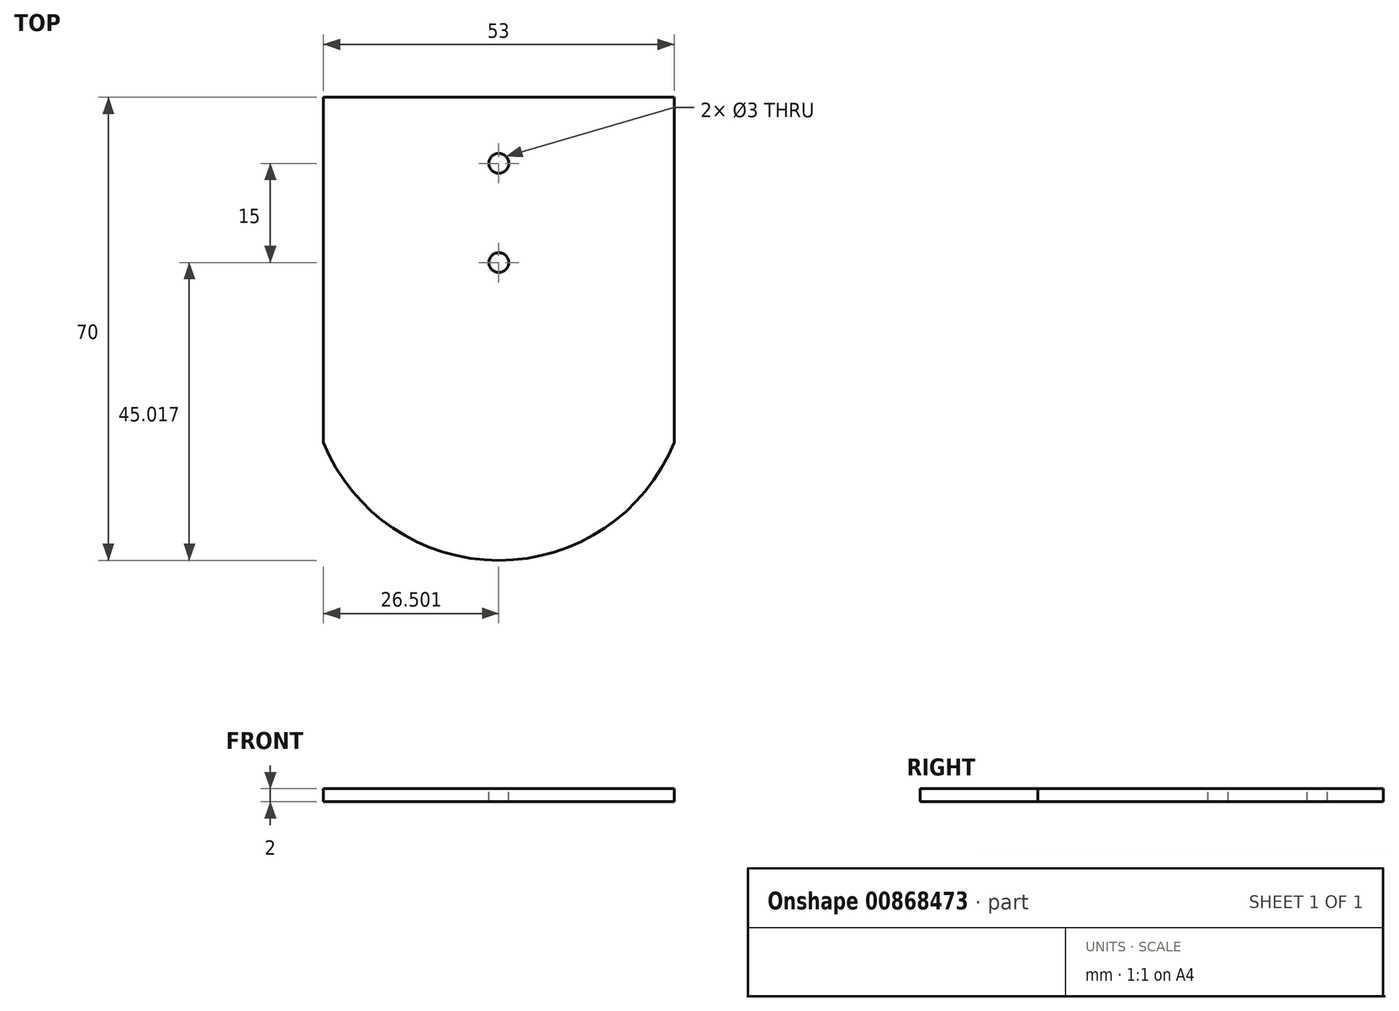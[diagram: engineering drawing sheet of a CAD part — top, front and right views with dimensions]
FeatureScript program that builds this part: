
annotation { "Feature Type Name" : "Feature", "Feature Type Description" : "" }
export const myFeature = defineFeature(function(context is Context, id is Id, definition is map)
    precondition{}
    {
        {
            var Q0;
            Q0=qCreatedBy(makeId("Top.planeOp"), FACE);
            var sketch = newSketch(context, id + "F0", { "sketchPlane" : qUnion([Q0])});
            skLineSegment(sketch, "E0", {"start": v(-38.9, 16.27) * mm, "end": v(14.1, 16.27) * mm});
            skLineSegment(sketch, "E1", {"start": v(-12.4, 16.27) * mm, "end": v(-12.4, -53.73) * mm, "construction": true});
            skLineSegment(sketch, "E2", {"start": v(-38.9, 16.27) * mm, "end": v(-38.9, -35.93) * mm});
            skLineSegment(sketch, "E3", {"start": v(14.1, 16.27) * mm, "end": v(14.1, -35.93) * mm});
            skPoint(sketch, "E4", {"position": v(-38.9, -35.93) * mm});
            skLineSegment(sketch, "E5", {"start": v(-38.9, -35.93) * mm, "end": v(14.1, -35.93) * mm, "construction": true});
            skArc(sketch, "E6", {"start": v(-38.9, -35.93) * mm, "mid": v(-12.4, -53.73) * mm, "end": v(14.1, -35.93) * mm});
            skPoint(sketch, "E7.orphan", {"position": v(-38.9, -53.73) * mm});
            skPoint(sketch, "E8.orphan", {"position": v(14.1, -53.73) * mm});
            skCircle(sketch, "E9", {"center": v(-12.4, 6.29) * mm, "radius": 1.5 * mm});
            skCircle(sketch, "E10", {"center": v(-12.4, -8.71) * mm, "radius": 1.5 * mm});
            skArc(sketch, "E11", {"start": v(-6.57, 9.18) * mm, "mid": v(-6.19, 10.88) * mm, "end": v(-6.42, 12.62) * mm, "construction": true});
            skLineSegment(sketch, "E12", {"start": v(-6.42, 12.62) * mm, "end": v(-7.1, 14.76) * mm, "construction": true});
            skArc(sketch, "E13", {"start": v(-22.4, 6.29) * mm, "mid": v(-17.25, 15.04) * mm, "end": v(-7.1, 14.76) * mm, "construction": true});
            skLineSegment(sketch, "E14", {"start": v(-22.4, -8.71) * mm, "end": v(-22.4, 6.29) * mm, "construction": true});
            skArc(sketch, "E15", {"start": v(-2.4, -8.71) * mm, "mid": v(-12.4, -18.71) * mm, "end": v(-22.4, -8.71) * mm, "construction": true});
            skLineSegment(sketch, "E16", {"start": v(-2.4, -8.71) * mm, "end": v(-2.4, 6.29) * mm, "construction": true});
            skArc(sketch, "E17", {"start": v(-2.6, 8.28) * mm, "mid": v(-2.46, 7.29) * mm, "end": v(-2.4, 6.29) * mm, "construction": true});
            skLineSegment(sketch, "E18", {"start": v(-7.02, -2.3) * mm, "end": v(-2.6, 8.28) * mm, "construction": true});
            skArc(sketch, "E19", {"start": v(-7.02, -2.3) * mm, "mid": v(-7.31, -3.25) * mm, "end": v(-7.4, -4.23) * mm, "construction": true});
            skLineSegment(sketch, "E20", {"start": v(-7.4, -4.71) * mm, "end": v(-7.4, -4.23) * mm, "construction": true});
            skLineSegment(sketch, "E21", {"start": v(-17.4, -4.71) * mm, "end": v(-7.4, -4.71) * mm, "construction": true});
            skLineSegment(sketch, "E22", {"start": v(-17.4, -4.71) * mm, "end": v(-17.4, 2.29) * mm, "construction": true});
            skLineSegment(sketch, "E23", {"start": v(-17.4, 2.29) * mm, "end": v(-12.77, 2.29) * mm, "construction": true});
            skArc(sketch, "E24", {"start": v(-12.77, 2.29) * mm, "mid": v(-10, 3.13) * mm, "end": v(-8.16, 5.36) * mm, "construction": true});
            skLineSegment(sketch, "E25", {"start": v(-8.16, 5.36) * mm, "end": v(-6.57, 9.18) * mm, "construction": true});
            skSolve(sketch);
        }
        {
            var Q0;
            Q0 = qSketchRegion(id + "F0", true);
            extrude(context, id + "F1", {"entities" : qUnion([Q0]), "oppositeDirection" : true, "depth" : 2 * mm, "offsetDistance" : 25 * mm});
        }
    });
